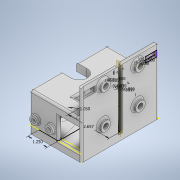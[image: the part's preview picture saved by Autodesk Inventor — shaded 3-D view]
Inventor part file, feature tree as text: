
AUTODESK INVENTOR PART (.ipt)
format: ipt  version: 2020 (Build 240168000, 168)  size: 585,216 bytes
history: native  units: in
note: dims shown in document units (in); Inventor stores cm internally (conversion verified against a paired STEP export)
features: sketch x18, extrude x15, hole x5, fillet x3, mirror x2, plane x1
ambient origin geometry x8: Origin, YZ Plane, XZ Plane, XY Plane, X Axis, Y Axis, Z Axis, Center Point
bodies: Solid1 (feature_tree)
feature tree (44):
  extrude  "Extrusion1"  Depth=5.0299in
  extrude  "Extrusion2"  Depth=0.375in
  extrude  "Extrusion3"  Depth=2.8543in
  sketch  "Sketch5"  dims[d24=5.315in d25=4.5472in]
  extrude  "Extrusion4"  Depth=4.5472in
  extrude  "Extrusion5"  Depth=0.25in
  extrude  "Extrusion6"  Depth=2.6575in
  hole  "Hole2"  [1 undecoded]
  extrude  "Extrusion7"  Depth=0.5in
  extrude  "Extrusion8"  Depth=1.5in
  extrude  "Extrusion9"  Depth=0.312in
  extrude  "Extrusion10"  Depth=0.312in
  hole  "Hole3"  [1 undecoded]
  extrude  "Extrusion11"  Depth=1.5in TaperAngle=0.0deg
  extrude  "Extrusion12"  Depth=1.125in
  hole  "Hole4"  [1 undecoded]
  sketch  "Sketch17"  dims[d61=1.49in d62=2.25in]
  extrude  "Extrusion13"  TaperAngle=90.0deg  [1 undecoded]
  hole  "Hole5"  [1 undecoded]
  plane  "Work Plane1"
  mirror  "Mirror1"
  extrude  "Extrusion14"  TaperAngle=0.0deg  [1 undecoded]
  fillet  "Fillet1"  Radius=0.625in
  sketch  "Sketch20"  dims[d67=0.332in d68=0.375in d69=0.119in d70=0.25in d71=0.5635in d72=0.375in d73=0.0in d74=0.0in d75=0.0in d76=0.625in d77=0.625in d78=0.625in d79=0.625in d80=0.2in d81=0.0in d82=0.21in d83=1.125in d84=0.185in d85=0.37in d86=0.09in d87=0.375in d88=0.119in d89=0.25in d90=0.5635in d91=0.375in d92=0.0in d93=0.375in d94=0.0in d95=0.25in d96=0.5in d97=0.375in d98=0.125in d99=0.0in d100=0.129in d101=0.198in d102=0.225in d103=0.188in d104=0.5635in d105=0.375in d106=0.0in d107=0.125in d108=0.125in d109=1.0in d110=1.0in d111=0.5in d112=1.5in d113=0.0in d114=0.931in d115=0.5in d116=1.0in d117=0.0in d120=0.1875in d121=0.0in d122=0.0625in d123=0.266in d124=0.75in d125=0.438in d126=0.25in d127=0.5635in d128=0.25in d129=0.0in d130=0.5in d131=90.0deg d132=0.5in d133=90.0deg d134=0.5in d135=0.5in d136=0.0625in]
  extrude  "Extrusion15"  Depth=0.0625in
  fillet  "Fillet2"  Radius=0.625in
  hole  "Hole6"  [1 undecoded]
  mirror  "Mirror2"
  fillet  "Fillet3"  Radius=0.2in
  sketch  "Sketch18"  dims[d63=2.25in d64=90.0deg]
  sketch  "Sketch1"  dims[d0=3.3654in d1=5.0299in]
  sketch  "Sketch3"  dims[d3=45.0deg d4=0.375in]
  sketch  "Sketch4"  dims[d5=0.5in d6=0.0in d23=2.8543in]
  sketch  "Sketch6"  dims[d26=0.1in d27=0.0in d28=0.25in]
  sketch  "Sketch7"  dims[d29=0.1in d30=0.0in d31=2.6575in]
  sketch  "Sketch9"  dims[d32=1.05in d33=1.25in]
  sketch  "Sketch10"  dims[d34=1.9685in d35=0.0in d36=0.5in]
  sketch  "Sketch11"  dims[d37=5.03in d38=0.0in d39=1.5in]
  sketch  "Sketch12"  dims[d40=1.0in d41=0.0in d42=0.312in]
  sketch  "Sketch13"  dims[d43=0.0in d44=0.312in]
  sketch  "Sketch14"  dims[d45=0.177in d46=0.75in d47=0.385in d48=0.25in d49=0.5635in d50=1.378in d51=0.0in d52=1.9685in d53=0.0in]
  sketch  "Sketch15"  dims[d54=1.9685in d55=0.0in d56=1.5in d57=0.0in]
  sketch  "Sketch16"  dims[d58=3.75in d59=0.0in d60=1.125in]
  sketch  "Sketch19"  dims[d65=2.25in d66=90.0deg]
note: 7 required parameter values undecoded (feature->parameter linkage not recoverable at this tier; creation-order binding heuristic only, values carry confidence <= 0.55)
